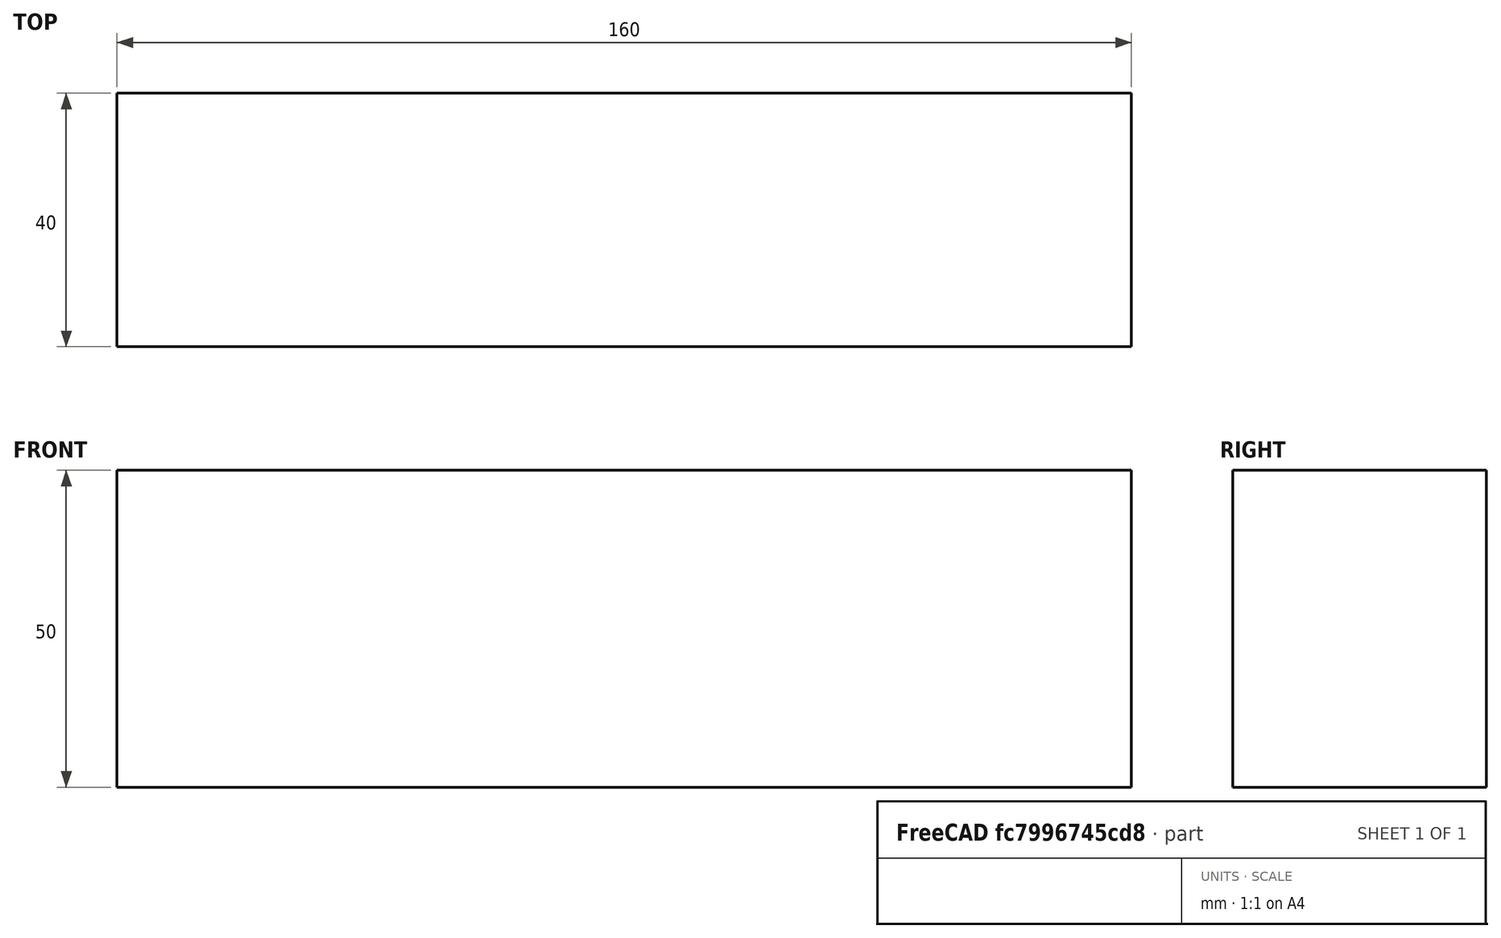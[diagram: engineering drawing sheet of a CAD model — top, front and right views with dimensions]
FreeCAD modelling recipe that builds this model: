
FCSTD DOCUMENT  (FreeCAD 0.15R4671 (Git))
Label: Flat Bar 160x40 EN10058 S235JR
License: All rights reserved
LicenseURL: http://en.wikipedia.org/wiki/All_rights_reserved
objects: Sketcher::SketchObject×1, Part::Extrusion×1
note: 2 computed .brp shape members not serialized (recipe doc carries the construction recipe); baked Part::Feature solids carry a one-line shape summary decoded from their .brp

FEATURE [Sketcher::SketchObject] Sketch
  sketch-geometry (4):
    g0: LineSegment StartX=-80 StartY=-20 StartZ=0 EndX=80 EndY=-20 EndZ=0
    g1: LineSegment StartX=80 StartY=-20 StartZ=0 EndX=80 EndY=20 EndZ=0
    g2: LineSegment StartX=80 StartY=20 StartZ=0 EndX=-80 EndY=20 EndZ=0
    g3: LineSegment StartX=-80 StartY=20 StartZ=0 EndX=-80 EndY=-20 EndZ=0
  constraints (12):
    c: Coincident(g0,g1)
    c: Coincident(g1,g2)
    c: Coincident(g2,g3)
    c: Coincident(g3,g0)
    c: Horizontal(g0)
    c: Horizontal(g2)
    c: Vertical(g1)
    c: Vertical(g3)
    c: Symmetric(g1,g2,g-2)
    c: Symmetric(g0,g1,g-1)
    c: DistanceY(g1) = 40
    c: DistanceX(g0) = 160
FEATURE [Part::Extrusion] Extrude  label="Flat Bar 160x40 EN10058 S235JR"
  Base = -> Sketch
  Dir = (0,0,50)
  Solid = true
